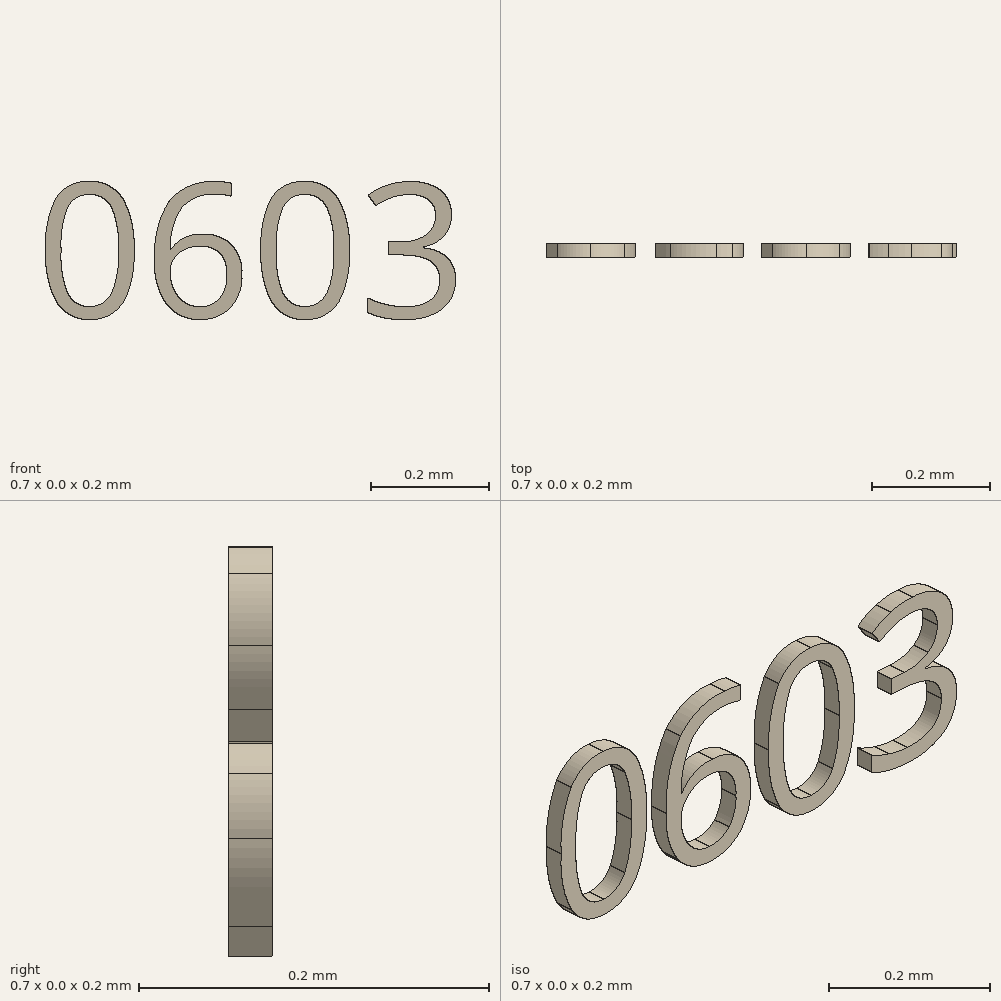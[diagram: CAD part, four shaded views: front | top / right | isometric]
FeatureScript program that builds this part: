
annotation { "Feature Type Name" : "Feature", "Feature Type Description" : "" }
export const myFeature = defineFeature(function(context is Context, id is Id, definition is map)
    precondition{}
    {
        {
            var Q0;
            Q0=qCreatedBy(makeId("Front.planeOp"),FACE);
            var sketch = newSketch(context, id + "F0", { "sketchPlane" : qUnion([Q0])});
            skText(sketch, "E0", { "text": "0603", "fontName": "OpenSans-Regular.ttf"});
            const initialGuessF0  = {"E0": [-0.00032, 8e-05, 1, 0, 0.00023]};
            skSetInitialGuess(sketch, initialGuessF0);
            skSolve(sketch);
        }
        {
            var Q0;
            Q0=qSketchRegion(id+"F0",true);
            extrude(context, id + "F1", {"entities" : qUnion([Q0]), "depth" : 0.03 * mm});
        }
    });
